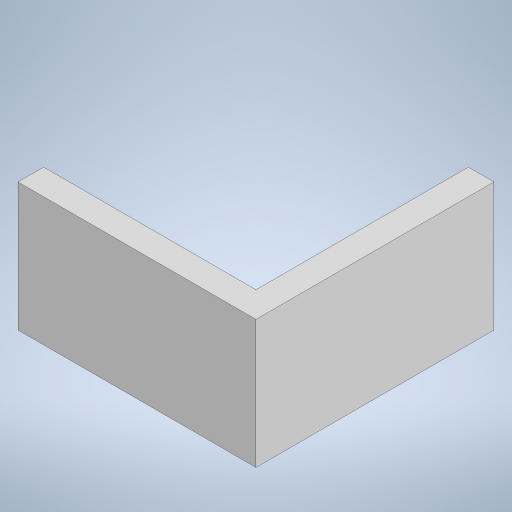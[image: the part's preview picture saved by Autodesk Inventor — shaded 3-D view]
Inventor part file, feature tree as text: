
AUTODESK INVENTOR PART (.ipt)
format: ipt  version: 2024.2 (Build 282272000, 272)  size: 209,920 bytes
history: native  units: mm
features: extrude x2, sketch x2
ambient origin geometry x8: Origin, YZ Plane, XZ Plane, XY Plane, X Axis, Y Axis, Z Axis, Center Point
bodies: Solid1 (feature_tree)
feature tree (4):
  extrude  "Extrusion1"  Depth=4.0mm
  extrude  "Extrusion2"  Depth=16.7mm
  sketch  "Sketch1"  dims[d0=16.7mm d1=4.0mm]
  sketch  "Sketch2"  dims[d2=4.0mm d3=16.7mm d4=5.0mm d5=0.0mm d6=1.8mm d7=1.8mm d8=16.7mm d9=4.0mm d10=0.0mm]
